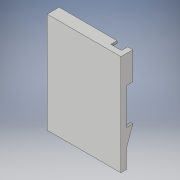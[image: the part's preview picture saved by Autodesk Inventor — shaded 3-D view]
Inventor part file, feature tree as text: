
AUTODESK INVENTOR PART (.ipt)
format: ipt  version: 2017.3 (Build 213256000, 256)  size: 203,264 bytes
history: native  units: mm
features: extrude x8, sketch x8, projected_geometry x6
ambient origin geometry x8: Origin, YZ Plane, XZ Plane, XY Plane, X Axis, Y Axis, Z Axis, Center Point
bodies: Solid1 (feature_tree)
feature tree (22):
  extrude  "Extrusion1"  Depth=81.82mm
  extrude  "Extrusion2"  Depth=2.0mm
  extrude  "Extrusion3"  Depth=2.0mm
  extrude  "Extrusion4"  Depth=2.0mm
  extrude  "Extrusion5"  Depth=2.0mm
  extrude  "Extrusion6"  Depth=2.2mm TaperAngle=0.0deg
  extrude  "Extrusion7"  Depth=10.2mm TaperAngle=0.0deg
  extrude  "Extrusion8"  Depth=9.05mm
  sketch  "Sketch1"  dims[d0=58.83mm d1=81.82mm]
  sketch  "Sketch2"  dims[d2=1.0mm d3=0.0mm d4=2.0mm]
  sketch  "Sketch3"  dims[d5=2.0mm d6=2.0mm]
  projected_geometry  "Projected Loop3"
  sketch  "Sketch4"  dims[d7=2.0mm d8=2.0mm]
  projected_geometry  "Projected Loop4"
  sketch  "Sketch5"  dims[d9=2.0mm d10=2.0mm]
  sketch  "Sketch7"  dims[d11=2.0mm d12=2.2mm d13=0.0mm]
  sketch  "Sketch8"  dims[d14=2.0mm d15=10.2mm d16=0.0mm]
  projected_geometry  "Projected Loop7"
  sketch  "Sketch9"  dims[d17=2.3mm d18=9.05mm d19=7.0mm d20=0.0mm d21=21.65mm d22=31.1mm d23=7.0mm d24=0.0mm d25=1.6mm d26=13.65mm d27=90.0deg d28=7.0mm d29=61.0mm d30=0.0mm d31=0.0mm d32=63.0mm d33=0.0mm d34=1.6mm d35=0.0mm]
  projected_geometry  "Projected Loop8"
  projected_geometry  "Projected Loop9"
  projected_geometry  "Project Cut Edges2"
